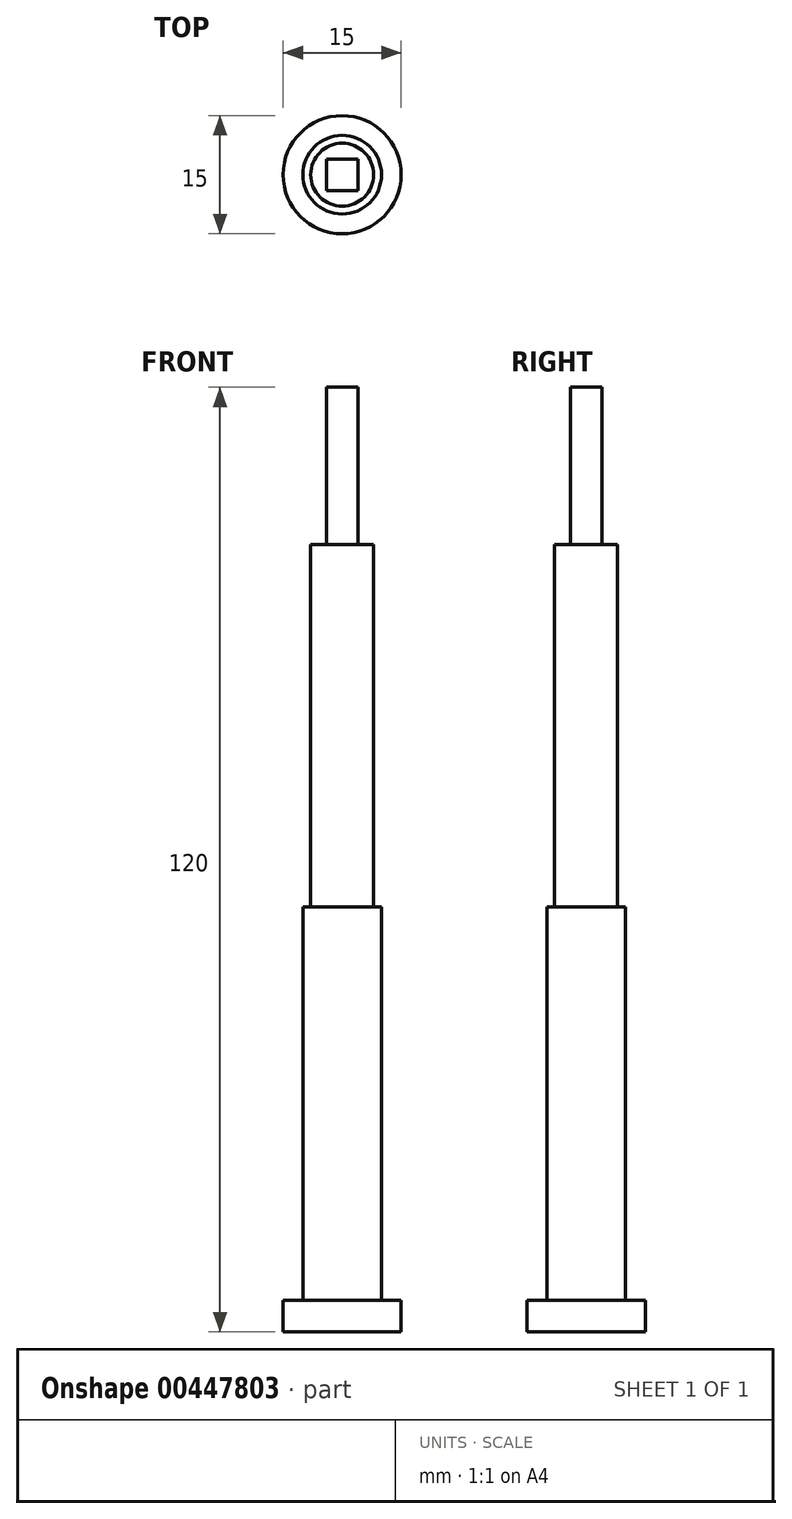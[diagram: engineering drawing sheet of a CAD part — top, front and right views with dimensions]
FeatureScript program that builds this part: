
annotation { "Feature Type Name" : "Feature", "Feature Type Description" : "" }
export const myFeature = defineFeature(function(context is Context, id is Id, definition is map)
    precondition{}
    {
        {
            var Q0;
            Q0=qCreatedBy(makeId("Top.planeOp"),FACE);
            var sketch = newSketch(context, id + "F0", { "sketchPlane" : qUnion([Q0])});
            skCircle(sketch, "E0", {"center": v(0, 0) * mm, "radius": 7.5 * mm});
            skSolve(sketch);
        }
        {
            var Q0;
            Q0=qSketchRegion(id+"F0",true);
            extrude(context, id + "F1", {"entities" : qUnion([Q0]), "depth" : 4 * mm});
        }
        {
            var Q0;
            Q0=qCreatedBy(makeId("Top.planeOp"),FACE);
            var sketch = newSketch(context, id + "F2", { "sketchPlane" : qUnion([Q0])});
            skCircle(sketch, "E1", {"center": v(0, 0) * mm, "radius": 5 * mm});
            skSolve(sketch);
        }
        {
            var Q0;
            Q0=qSketchRegion(id+"F2",true);
            extrude(context, id + "F3", {"entities" : qUnion([Q0]), "operationType" : NewBodyOperationType.ADD, "depth" : 54 * mm});
        }
        {
            var Q0;
            Q0=makeQuery(id+"F3.opExtrude","CAP_FACE",FACE,{"disambiguationData":[OSD([sQuery(id+"F2.wireOp",EDGE,"E1")])],"isStart":false});
            var sketch = newSketch(context, id + "F4", { "sketchPlane" : qUnion([Q0])});
            skCircle(sketch, "E2", {"center": v(0, 0) * mm, "radius": 4 * mm});
            skSolve(sketch);
        }
        {
            var Q0;
            Q0 = qSketchRegion(id + "F4", true);
            extrude(context, id + "F5", {"entities" : qUnion([Q0]), "operationType" : NewBodyOperationType.ADD, "depth" : 46 * mm});
        }
        {
            var Q0;
            Q0=makeQuery(id+"F5.opExtrude","CAP_FACE",FACE,{"disambiguationData":[OSD([sQuery(id+"F4.wireOp",EDGE,"E2")])],"isStart":false});
            var sketch = newSketch(context, id + "F6", { "sketchPlane" : qUnion([Q0])});
            skLineSegment(sketch, "E3.bottom", {"start": v(-2, 2) * mm, "end": v(2, 2) * mm});
            skLineSegment(sketch, "E3.top", {"start": v(-2, -2) * mm, "end": v(2, -2) * mm});
            skLineSegment(sketch, "E3.left", {"start": v(-2, 2) * mm, "end": v(-2, -2) * mm});
            skLineSegment(sketch, "E3.right", {"start": v(2, 2) * mm, "end": v(2, -2) * mm});
            skSolve(sketch);
        }
        {
            var Q0;
            Q0 = qSketchRegion(id + "F6", true);
            extrude(context, id + "F7", {"entities" : qUnion([Q0]), "operationType" : NewBodyOperationType.ADD, "depth" : 20 * mm});
        }
    });
